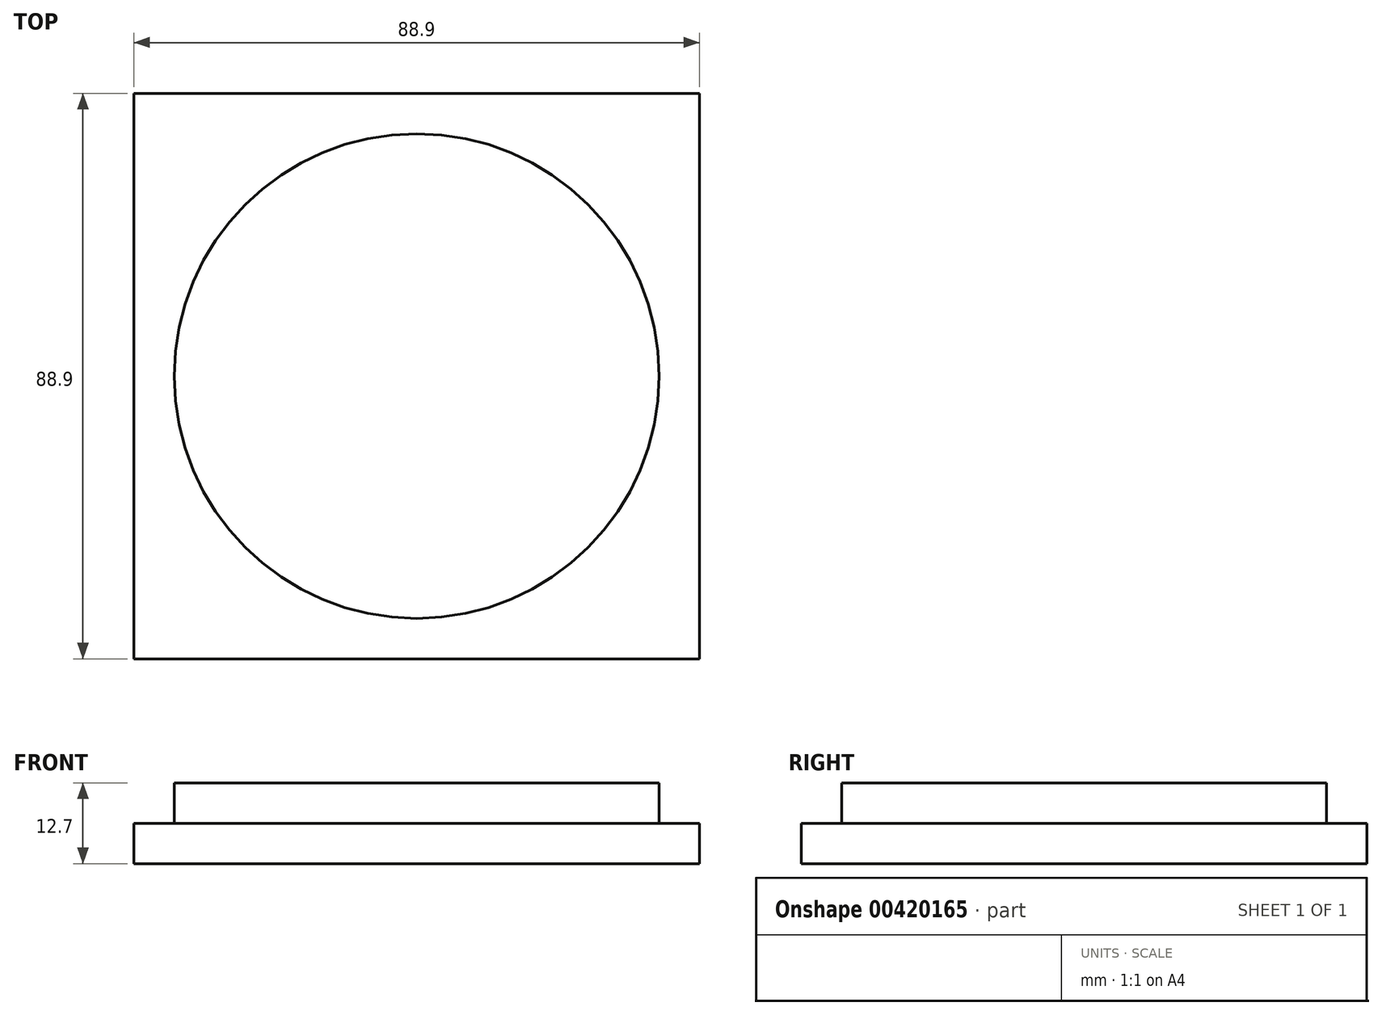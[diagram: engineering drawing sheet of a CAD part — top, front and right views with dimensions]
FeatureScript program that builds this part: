
annotation { "Feature Type Name" : "Feature", "Feature Type Description" : "" }
export const myFeature = defineFeature(function(context is Context, id is Id, definition is map)
    precondition{}
    {
        {
            var Q0;
            Q0=qCreatedBy(makeId("Top.planeOp"),FACE);
            var sketch = newSketch(context, id + "F0", { "sketchPlane" : qUnion([Q0])});
            skCircle(sketch, "E0", {"center": v(0, 0) * mm, "radius": 38.1 * mm});
            skSolve(sketch);
        }
        {
            var Q0;
            Q0 = qSketchRegion(id + "F0", true);
            extrude(context, id + "F1", {"entities" : qUnion([Q0]), "depth" : 6.35 * mm});
        }
        {
            var Q0;
            Q0=qCreatedBy(makeId("Top.planeOp"),FACE);
            var sketch = newSketch(context, id + "F2", { "sketchPlane" : qUnion([Q0])});
            skLineSegment(sketch, "E1.bottom", {"start": v(-44.45, 44.45) * mm, "end": v(44.45, 44.45) * mm});
            skLineSegment(sketch, "E1.top", {"start": v(-44.45, -44.45) * mm, "end": v(44.45, -44.45) * mm});
            skLineSegment(sketch, "E1.left", {"start": v(-44.45, 44.45) * mm, "end": v(-44.45, -44.45) * mm});
            skLineSegment(sketch, "E1.right", {"start": v(44.45, 44.45) * mm, "end": v(44.45, -44.45) * mm});
            skPoint(sketch, "E2", {"position": v(0, 44.45) * mm});
            skPoint(sketch, "E3", {"position": v(-44.45, 0) * mm});
            skSolve(sketch);
        }
        {
            var Q0;
            Q0 = qSketchRegion(id + "F2", true);
            extrude(context, id + "F3", {"entities" : qUnion([Q0]), "operationType" : NewBodyOperationType.ADD, "oppositeDirection" : true, "depth" : 6.35 * mm});
        }
    });
